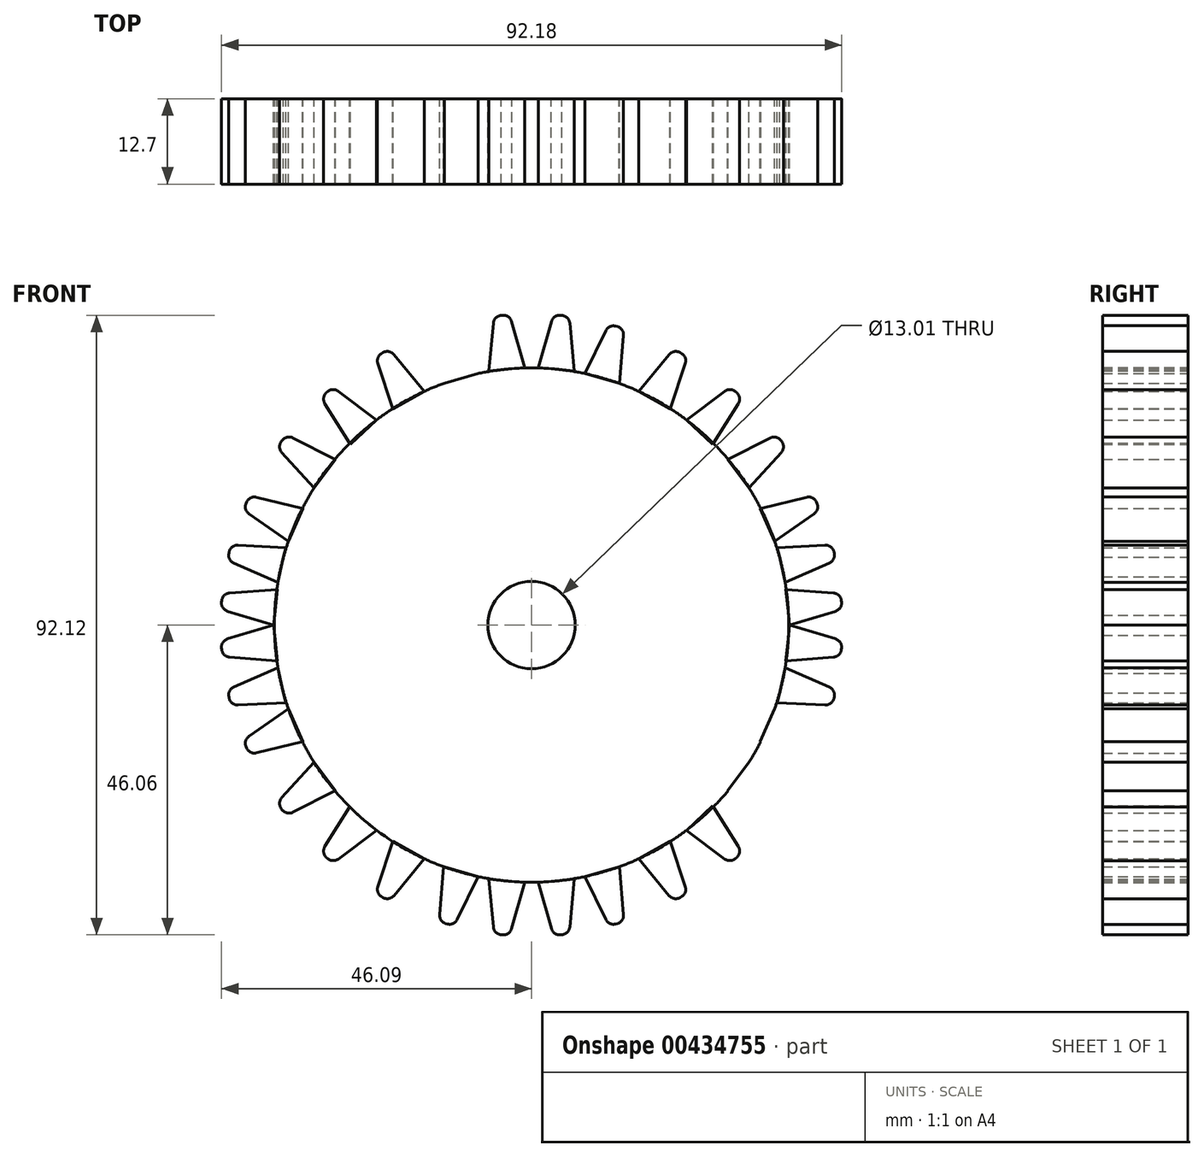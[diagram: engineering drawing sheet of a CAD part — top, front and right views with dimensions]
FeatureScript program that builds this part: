
annotation { "Feature Type Name" : "Feature", "Feature Type Description" : "" }
export const myFeature = defineFeature(function(context is Context, id is Id, definition is map)
    precondition{}
    {
        {
            var Q0;
            Q0=qCreatedBy(makeId("Front.planeOp"),FACE);
            var sketch = newSketch(context, id + "F0", { "sketchPlane" : qUnion([Q0])});
            skCircle(sketch, "E0", {"center": v(0, 0) * mm, "radius": 38.23 * mm});
            skLineSegment(sketch, "E1", {"start": v(4.32, 46.06) * mm, "end": v(4.54, 46.04) * mm});
            skLineSegment(sketch, "E2", {"start": v(5.69, 44.9) * mm, "end": v(6.35, 37.78) * mm});
            skLineSegment(sketch, "E3", {"start": v(6.35, 37.78) * mm, "end": v(1.04, 38.3) * mm});
            skLineSegment(sketch, "E4", {"start": v(1.04, 38.3) * mm, "end": v(2.98, 45.14) * mm});
            skArc(sketch, "E5.filletArc", {"start": v(4.32, 46.06) * mm, "mid": v(3.48, 45.84) * mm, "end": v(2.98, 45.14) * mm});
            skArc(sketch, "E6.filletArc", {"start": v(5.69, 44.9) * mm, "mid": v(5.32, 45.67) * mm, "end": v(4.54, 46.04) * mm});
            skLineSegment(sketch, "E7", {"start": v(-38.23, 0) * mm, "end": v(38.23, 0) * mm});
            skLineSegment(sketch, "E8", {"start": v(0, 0) * mm, "end": v(0, 38.07) * mm});
            skLineSegment(sketch, "E9", {"start": v(0, 0) * mm, "end": v(0, -38.23) * mm});
            skLineSegment(sketch, "E10", {"start": v(12.53, 44.44) * mm, "end": v(12.74, 44.38) * mm});
            skLineSegment(sketch, "E11", {"start": v(13.66, 43.05) * mm, "end": v(13.06, 35.93) * mm});
            skLineSegment(sketch, "E12", {"start": v(13.06, 35.93) * mm, "end": v(7.92, 37.38) * mm});
            skLineSegment(sketch, "E13", {"start": v(7.92, 37.38) * mm, "end": v(11.04, 43.77) * mm});
            skArc(sketch, "E14.filletArc", {"start": v(12.53, 44.44) * mm, "mid": v(11.66, 44.38) * mm, "end": v(11.04, 43.77) * mm});
            skArc(sketch, "E15.filletArc", {"start": v(13.66, 43.05) * mm, "mid": v(13.44, 43.88) * mm, "end": v(12.74, 44.38) * mm});
            skLineSegment(sketch, "E16", {"start": v(22.07, 40.52) * mm, "end": v(22.27, 40.41) * mm});
            skLineSegment(sketch, "E17", {"start": v(22.85, 38.9) * mm, "end": v(20.59, 32.13) * mm});
            skLineSegment(sketch, "E18", {"start": v(20.59, 32.13) * mm, "end": v(15.94, 34.74) * mm});
            skLineSegment(sketch, "E19", {"start": v(15.94, 34.74) * mm, "end": v(20.47, 40.23) * mm});
            skArc(sketch, "E20.filletArc", {"start": v(22.07, 40.52) * mm, "mid": v(21.22, 40.67) * mm, "end": v(20.47, 40.23) * mm});
            skArc(sketch, "E21.filletArc", {"start": v(22.85, 38.9) * mm, "mid": v(22.83, 39.76) * mm, "end": v(22.27, 40.41) * mm});
            skLineSegment(sketch, "E22", {"start": v(30.35, 34.68) * mm, "end": v(30.52, 34.53) * mm});
            skLineSegment(sketch, "E23", {"start": v(30.73, 32.92) * mm, "end": v(26.93, 26.87) * mm});
            skLineSegment(sketch, "E24", {"start": v(26.93, 26.87) * mm, "end": v(23.03, 30.51) * mm});
            skLineSegment(sketch, "E25", {"start": v(23.03, 30.51) * mm, "end": v(28.73, 34.77) * mm});
            skArc(sketch, "E26.filletArc", {"start": v(30.35, 34.68) * mm, "mid": v(29.56, 35.02) * mm, "end": v(28.73, 34.77) * mm});
            skArc(sketch, "E27.filletArc", {"start": v(30.73, 32.92) * mm, "mid": v(30.9, 33.76) * mm, "end": v(30.52, 34.53) * mm});
            skLineSegment(sketch, "E28", {"start": v(37.07, 27.46) * mm, "end": v(37.2, 27.29) * mm});
            skLineSegment(sketch, "E29", {"start": v(37.13, 25.67) * mm, "end": v(32.34, 20.38) * mm});
            skLineSegment(sketch, "E30", {"start": v(32.34, 20.38) * mm, "end": v(29.14, 24.63) * mm});
            skLineSegment(sketch, "E31", {"start": v(29.14, 24.63) * mm, "end": v(35.49, 27.83) * mm});
            skArc(sketch, "E32.filletArc", {"start": v(37.07, 27.46) * mm, "mid": v(36.35, 27.93) * mm, "end": v(35.49, 27.83) * mm});
            skArc(sketch, "E33.filletArc", {"start": v(37.13, 25.67) * mm, "mid": v(37.46, 26.47) * mm, "end": v(37.2, 27.29) * mm});
            skLineSegment(sketch, "E34", {"start": v(42.34, 18.3) * mm, "end": v(42.43, 18.1) * mm});
            skLineSegment(sketch, "E35", {"start": v(42, 16.54) * mm, "end": v(36.14, 12.44) * mm});
            skLineSegment(sketch, "E36", {"start": v(36.14, 12.44) * mm, "end": v(33.97, 17.31) * mm});
            skLineSegment(sketch, "E37", {"start": v(33.97, 17.31) * mm, "end": v(40.87, 19.01) * mm});
            skArc(sketch, "E38.filletArc", {"start": v(42.34, 18.3) * mm, "mid": v(41.73, 18.92) * mm, "end": v(40.87, 19.01) * mm});
            skArc(sketch, "E39.filletArc", {"start": v(42, 16.54) * mm, "mid": v(42.5, 17.24) * mm, "end": v(42.43, 18.1) * mm});
            skLineSegment(sketch, "E40", {"start": v(44.94, 10.9) * mm, "end": v(45, 10.68) * mm});
            skArc(sketch, "E41.filletArc", {"start": v(44.27, 9.23) * mm, "mid": v(44.9, 9.82) * mm, "end": v(45, 10.68) * mm});
            skLineSegment(sketch, "E42", {"start": v(44.27, 9.23) * mm, "end": v(37.74, 6.33) * mm});
            skLineSegment(sketch, "E43", {"start": v(37.74, 6.33) * mm, "end": v(36.54, 11.53) * mm});
            skLineSegment(sketch, "E44", {"start": v(36.54, 11.53) * mm, "end": v(43.64, 11.88) * mm});
            skArc(sketch, "E45.filletArc", {"start": v(44.94, 10.9) * mm, "mid": v(44.47, 11.62) * mm, "end": v(43.64, 11.88) * mm});
            skLineSegment(sketch, "E46", {"start": v(46.06, 3.63) * mm, "end": v(46.09, 3.4) * mm});
            skLineSegment(sketch, "E47", {"start": v(45.19, 2.06) * mm, "end": v(38.35, 0) * mm});
            skLineSegment(sketch, "E48", {"start": v(38.35, 0) * mm, "end": v(37.8, 5.3) * mm});
            skLineSegment(sketch, "E49", {"start": v(37.8, 5.3) * mm, "end": v(44.9, 4.76) * mm});
            skArc(sketch, "E50.filletArc", {"start": v(46.06, 3.63) * mm, "mid": v(45.69, 4.4) * mm, "end": v(44.9, 4.76) * mm});
            skArc(sketch, "E51.filletArc", {"start": v(45.19, 2.06) * mm, "mid": v(45.88, 2.57) * mm, "end": v(46.09, 3.4) * mm});
            skLineSegment(sketch, "E52.MirrorCS", {"start": v(-4.32, 46.06) * mm, "end": v(-4.54, 46.04) * mm});
            skArc(sketch, "E53.MirrorCS", {"start": v(-4.32, 46.06) * mm, "mid": v(-3.48, 45.84) * mm, "end": v(-2.98, 45.14) * mm});
            skLineSegment(sketch, "E54.MirrorCS", {"start": v(-1.04, 38.3) * mm, "end": v(-2.98, 45.14) * mm});
            skLineSegment(sketch, "E55.MirrorCS", {"start": v(-5.69, 44.9) * mm, "end": v(-6.35, 37.78) * mm});
            skArc(sketch, "E56.MirrorCS", {"start": v(-5.69, 44.9) * mm, "mid": v(-5.32, 45.67) * mm, "end": v(-4.54, 46.04) * mm});
            skLineSegment(sketch, "E57.MirrorCS", {"start": v(-6.35, 37.78) * mm, "end": v(-1.04, 38.3) * mm});
            skLineSegment(sketch, "E58.MirrorCS", {"start": v(-7.92, 37.38) * mm, "end": v(-11.04, 43.77) * mm});
            skArc(sketch, "E59.MirrorCS", {"start": v(-12.53, 44.44) * mm, "mid": v(-11.66, 44.38) * mm, "end": v(-11.04, 43.77) * mm});
            skArc(sketch, "E60.MirrorCS", {"start": v(-13.66, 43.05) * mm, "mid": v(-13.44, 43.88) * mm, "end": v(-12.74, 44.38) * mm});
            skLineSegment(sketch, "E61.MirrorCS", {"start": v(-13.66, 43.05) * mm, "end": v(-13.06, 35.93) * mm});
            skLineSegment(sketch, "E62.MirrorCS", {"start": v(-13.06, 35.93) * mm, "end": v(-7.92, 37.38) * mm});
            skLineSegment(sketch, "E63.MirrorCS", {"start": v(-12.53, 44.44) * mm, "end": v(-12.74, 44.38) * mm});
            skLineSegment(sketch, "E64.MirrorCS", {"start": v(-22.07, 40.52) * mm, "end": v(-22.27, 40.41) * mm});
            skArc(sketch, "E65.MirrorCS", {"start": v(-22.07, 40.52) * mm, "mid": v(-21.22, 40.67) * mm, "end": v(-20.47, 40.23) * mm});
            skArc(sketch, "E66.MirrorCS", {"start": v(-22.85, 38.9) * mm, "mid": v(-22.83, 39.76) * mm, "end": v(-22.27, 40.41) * mm});
            skLineSegment(sketch, "E67.MirrorCS", {"start": v(-22.85, 38.9) * mm, "end": v(-20.59, 32.13) * mm});
            skLineSegment(sketch, "E68.MirrorCS", {"start": v(-15.94, 34.74) * mm, "end": v(-20.47, 40.23) * mm});
            skLineSegment(sketch, "E69.MirrorCS", {"start": v(-20.59, 32.13) * mm, "end": v(-15.94, 34.74) * mm});
            skLineSegment(sketch, "E70.MirrorCS", {"start": v(-30.35, 34.68) * mm, "end": v(-30.52, 34.53) * mm});
            skArc(sketch, "E71.MirrorCS", {"start": v(-30.35, 34.68) * mm, "mid": v(-29.56, 35.02) * mm, "end": v(-28.73, 34.77) * mm});
            skArc(sketch, "E72.MirrorCS", {"start": v(-30.73, 32.92) * mm, "mid": v(-30.9, 33.76) * mm, "end": v(-30.52, 34.53) * mm});
            skLineSegment(sketch, "E73.MirrorCS", {"start": v(-30.73, 32.92) * mm, "end": v(-26.93, 26.87) * mm});
            skLineSegment(sketch, "E74.MirrorCS", {"start": v(-23.03, 30.51) * mm, "end": v(-28.73, 34.77) * mm});
            skLineSegment(sketch, "E75.MirrorCS", {"start": v(-37.13, 25.67) * mm, "end": v(-32.34, 20.38) * mm});
            skLineSegment(sketch, "E76.MirrorCS", {"start": v(-29.14, 24.63) * mm, "end": v(-35.49, 27.83) * mm});
            skArc(sketch, "E77.MirrorCS", {"start": v(-37.07, 27.46) * mm, "mid": v(-36.35, 27.93) * mm, "end": v(-35.49, 27.83) * mm});
            skArc(sketch, "E78.MirrorCS", {"start": v(-37.13, 25.67) * mm, "mid": v(-37.46, 26.47) * mm, "end": v(-37.2, 27.29) * mm});
            skLineSegment(sketch, "E79.MirrorCS", {"start": v(-32.34, 20.38) * mm, "end": v(-29.14, 24.63) * mm});
            skLineSegment(sketch, "E80.MirrorCS", {"start": v(-37.07, 27.46) * mm, "end": v(-37.2, 27.29) * mm});
            skLineSegment(sketch, "E81.MirrorCS", {"start": v(-33.97, 17.31) * mm, "end": v(-40.87, 19.01) * mm});
            skLineSegment(sketch, "E82.MirrorCS", {"start": v(-36.54, 11.53) * mm, "end": v(-43.64, 11.88) * mm});
            skLineSegment(sketch, "E83.MirrorCS", {"start": v(-37.8, 5.3) * mm, "end": v(-44.9, 4.76) * mm});
            skLineSegment(sketch, "E84.MirrorCS", {"start": v(-42.34, 18.3) * mm, "end": v(-42.43, 18.1) * mm});
            skArc(sketch, "E85.MirrorCS", {"start": v(-42, 16.54) * mm, "mid": v(-42.5, 17.24) * mm, "end": v(-42.43, 18.1) * mm});
            skArc(sketch, "E86.MirrorCS", {"start": v(-42.34, 18.3) * mm, "mid": v(-41.73, 18.92) * mm, "end": v(-40.87, 19.01) * mm});
            skLineSegment(sketch, "E87.MirrorCS", {"start": v(-42, 16.54) * mm, "end": v(-36.14, 12.44) * mm});
            skLineSegment(sketch, "E88.MirrorCS", {"start": v(-44.27, 9.23) * mm, "end": v(-37.74, 6.33) * mm});
            skArc(sketch, "E89.MirrorCS", {"start": v(-44.94, 10.9) * mm, "mid": v(-44.47, 11.62) * mm, "end": v(-43.64, 11.88) * mm});
            skArc(sketch, "E90.MirrorCS", {"start": v(-44.27, 9.23) * mm, "mid": v(-44.9, 9.82) * mm, "end": v(-45, 10.68) * mm});
            skLineSegment(sketch, "E91.MirrorCS", {"start": v(-44.94, 10.9) * mm, "end": v(-45, 10.68) * mm});
            skLineSegment(sketch, "E92.MirrorCS", {"start": v(-37.74, 6.33) * mm, "end": v(-36.54, 11.53) * mm});
            skLineSegment(sketch, "E93.MirrorCS", {"start": v(-45.19, 2.06) * mm, "end": v(-38.35, 0) * mm});
            skArc(sketch, "E94.MirrorCS", {"start": v(-45.19, 2.06) * mm, "mid": v(-45.88, 2.57) * mm, "end": v(-46.09, 3.4) * mm});
            skArc(sketch, "E95.MirrorCS", {"start": v(-46.06, 3.63) * mm, "mid": v(-45.69, 4.4) * mm, "end": v(-44.9, 4.76) * mm});
            skLineSegment(sketch, "E96.MirrorCS", {"start": v(-46.06, 3.63) * mm, "end": v(-46.09, 3.4) * mm});
            skLineSegment(sketch, "E97.MirrorCS", {"start": v(-38.35, 0) * mm, "end": v(-37.8, 5.3) * mm});
            skLineSegment(sketch, "E98.MirrorCS", {"start": v(-37.8, -5.3) * mm, "end": v(-44.9, -4.76) * mm});
            skLineSegment(sketch, "E99.MirrorCS", {"start": v(-45.19, -2.06) * mm, "end": v(-38.35, 0) * mm});
            skArc(sketch, "E100.MirrorCS", {"start": v(-45.19, -2.06) * mm, "mid": v(-45.88, -2.57) * mm, "end": v(-46.09, -3.4) * mm});
            skArc(sketch, "E101.MirrorCS", {"start": v(-46.06, -3.63) * mm, "mid": v(-45.69, -4.4) * mm, "end": v(-44.9, -4.76) * mm});
            skLineSegment(sketch, "E102.MirrorCS", {"start": v(-46.06, -3.63) * mm, "end": v(-46.09, -3.4) * mm});
            skLineSegment(sketch, "E103.MirrorCS", {"start": v(-44.94, -10.9) * mm, "end": v(-45, -10.68) * mm});
            skArc(sketch, "E104.MirrorCS", {"start": v(-44.27, -9.23) * mm, "mid": v(-44.9, -9.82) * mm, "end": v(-45, -10.68) * mm});
            skLineSegment(sketch, "E105.MirrorCS", {"start": v(-44.27, -9.23) * mm, "end": v(-37.74, -6.33) * mm});
            skLineSegment(sketch, "E106.MirrorCS", {"start": v(-36.54, -11.53) * mm, "end": v(-43.64, -11.88) * mm});
            skArc(sketch, "E107.MirrorCS", {"start": v(-44.94, -10.9) * mm, "mid": v(-44.47, -11.62) * mm, "end": v(-43.64, -11.88) * mm});
            skLineSegment(sketch, "E108.MirrorCS", {"start": v(-37.74, -6.33) * mm, "end": v(-36.54, -11.53) * mm});
            skLineSegment(sketch, "E109.MirrorCS", {"start": v(-42, -16.54) * mm, "end": v(-36.14, -12.44) * mm});
            skArc(sketch, "E110.MirrorCS", {"start": v(-42, -16.54) * mm, "mid": v(-42.5, -17.24) * mm, "end": v(-42.43, -18.1) * mm});
            skArc(sketch, "E111.MirrorCS", {"start": v(-42.34, -18.3) * mm, "mid": v(-41.73, -18.92) * mm, "end": v(-40.87, -19.01) * mm});
            skLineSegment(sketch, "E112.MirrorCS", {"start": v(-33.97, -17.31) * mm, "end": v(-40.87, -19.01) * mm});
            skLineSegment(sketch, "E113.MirrorCS", {"start": v(-42.34, -18.3) * mm, "end": v(-42.43, -18.1) * mm});
            skLineSegment(sketch, "E114.MirrorCS", {"start": v(-32.34, -20.38) * mm, "end": v(-29.14, -24.63) * mm});
            skLineSegment(sketch, "E115.MirrorCS", {"start": v(-37.13, -25.67) * mm, "end": v(-32.34, -20.38) * mm});
            skLineSegment(sketch, "E116.MirrorCS", {"start": v(-29.14, -24.63) * mm, "end": v(-35.49, -27.83) * mm});
            skArc(sketch, "E117.MirrorCS", {"start": v(-37.13, -25.67) * mm, "mid": v(-37.46, -26.47) * mm, "end": v(-37.2, -27.29) * mm});
            skArc(sketch, "E118.MirrorCS", {"start": v(-37.07, -27.46) * mm, "mid": v(-36.35, -27.93) * mm, "end": v(-35.49, -27.83) * mm});
            skLineSegment(sketch, "E119.MirrorCS", {"start": v(-37.07, -27.46) * mm, "end": v(-37.2, -27.29) * mm});
            skLineSegment(sketch, "E120.MirrorCS", {"start": v(-30.73, -32.92) * mm, "end": v(-26.93, -26.87) * mm});
            skArc(sketch, "E121.MirrorCS", {"start": v(-30.73, -32.92) * mm, "mid": v(-30.9, -33.76) * mm, "end": v(-30.52, -34.53) * mm});
            skArc(sketch, "E122.MirrorCS", {"start": v(-30.35, -34.68) * mm, "mid": v(-29.56, -35.02) * mm, "end": v(-28.73, -34.77) * mm});
            skLineSegment(sketch, "E123.MirrorCS", {"start": v(-23.03, -30.51) * mm, "end": v(-28.73, -34.77) * mm});
            skLineSegment(sketch, "E124.MirrorCS", {"start": v(-20.59, -32.13) * mm, "end": v(-15.94, -34.74) * mm});
            skLineSegment(sketch, "E125.MirrorCS", {"start": v(-22.85, -38.9) * mm, "end": v(-20.59, -32.13) * mm});
            skLineSegment(sketch, "E126.MirrorCS", {"start": v(-15.94, -34.74) * mm, "end": v(-20.47, -40.23) * mm});
            skArc(sketch, "E127.MirrorCS", {"start": v(-22.07, -40.52) * mm, "mid": v(-21.22, -40.67) * mm, "end": v(-20.47, -40.23) * mm});
            skArc(sketch, "E128.MirrorCS", {"start": v(-22.85, -38.9) * mm, "mid": v(-22.83, -39.76) * mm, "end": v(-22.27, -40.41) * mm});
            skLineSegment(sketch, "E129.MirrorCS", {"start": v(-22.07, -40.52) * mm, "end": v(-22.27, -40.41) * mm});
            skLineSegment(sketch, "E130.MirrorCS", {"start": v(-13.66, -43.05) * mm, "end": v(-13.06, -35.93) * mm});
            skArc(sketch, "E131.MirrorCS", {"start": v(-13.66, -43.05) * mm, "mid": v(-13.44, -43.88) * mm, "end": v(-12.74, -44.38) * mm});
            skArc(sketch, "E132.MirrorCS", {"start": v(-12.53, -44.44) * mm, "mid": v(-11.66, -44.38) * mm, "end": v(-11.04, -43.77) * mm});
            skLineSegment(sketch, "E133.MirrorCS", {"start": v(-7.92, -37.38) * mm, "end": v(-11.04, -43.77) * mm});
            skLineSegment(sketch, "E134.MirrorCS", {"start": v(-13.06, -35.93) * mm, "end": v(-7.92, -37.38) * mm});
            skLineSegment(sketch, "E135.MirrorCS", {"start": v(-5.69, -44.9) * mm, "end": v(-6.35, -37.78) * mm});
            skLineSegment(sketch, "E136.MirrorCS", {"start": v(-1.04, -38.3) * mm, "end": v(-2.98, -45.14) * mm});
            skLineSegment(sketch, "E137.MirrorCS", {"start": v(-12.53, -44.44) * mm, "end": v(-12.74, -44.38) * mm});
            skLineSegment(sketch, "E138.MirrorCS", {"start": v(-4.32, -46.06) * mm, "end": v(-4.54, -46.04) * mm});
            skArc(sketch, "E139.MirrorCS", {"start": v(-4.32, -46.06) * mm, "mid": v(-3.48, -45.84) * mm, "end": v(-2.98, -45.14) * mm});
            skArc(sketch, "E140.MirrorCS", {"start": v(-5.69, -44.9) * mm, "mid": v(-5.32, -45.67) * mm, "end": v(-4.54, -46.04) * mm});
            skLineSegment(sketch, "E141.MirrorCS", {"start": v(-6.35, -37.78) * mm, "end": v(-1.04, -38.3) * mm});
            skLineSegment(sketch, "E142.MirrorCS", {"start": v(-30.35, -34.68) * mm, "end": v(-30.52, -34.53) * mm});
            skLineSegment(sketch, "E143.MirrorCS", {"start": v(-26.93, 26.87) * mm, "end": v(-23.03, 30.51) * mm});
            skLineSegment(sketch, "E144.MirrorCS", {"start": v(-36.14, 12.44) * mm, "end": v(-33.97, 17.31) * mm});
            skLineSegment(sketch, "E145.MirrorCS", {"start": v(-36.14, -12.44) * mm, "end": v(-33.97, -17.31) * mm});
            skLineSegment(sketch, "E146.MirrorCS", {"start": v(-38.35, 0) * mm, "end": v(-37.8, -5.3) * mm});
            skLineSegment(sketch, "E147.MirrorCS", {"start": v(5.69, -44.9) * mm, "end": v(6.35, -37.78) * mm});
            skLineSegment(sketch, "E148.MirrorCS", {"start": v(1.04, -38.3) * mm, "end": v(2.98, -45.14) * mm});
            skArc(sketch, "E149.MirrorCS", {"start": v(4.32, -46.06) * mm, "mid": v(3.48, -45.84) * mm, "end": v(2.98, -45.14) * mm});
            skLineSegment(sketch, "E150.MirrorCS", {"start": v(4.32, -46.06) * mm, "end": v(4.54, -46.04) * mm});
            skArc(sketch, "E151.MirrorCS", {"start": v(5.69, -44.9) * mm, "mid": v(5.32, -45.67) * mm, "end": v(4.54, -46.04) * mm});
            skLineSegment(sketch, "E152.MirrorCS", {"start": v(13.66, -43.05) * mm, "end": v(13.06, -35.93) * mm});
            skLineSegment(sketch, "E153.MirrorCS", {"start": v(6.35, -37.78) * mm, "end": v(1.04, -38.3) * mm});
            skLineSegment(sketch, "E154.MirrorCS", {"start": v(7.92, -37.38) * mm, "end": v(11.04, -43.77) * mm});
            skArc(sketch, "E155.MirrorCS", {"start": v(12.53, -44.44) * mm, "mid": v(11.66, -44.38) * mm, "end": v(11.04, -43.77) * mm});
            skArc(sketch, "E156.MirrorCS", {"start": v(13.66, -43.05) * mm, "mid": v(13.44, -43.88) * mm, "end": v(12.74, -44.38) * mm});
            skLineSegment(sketch, "E157.MirrorCS", {"start": v(12.53, -44.44) * mm, "end": v(12.74, -44.38) * mm});
            skLineSegment(sketch, "E158.MirrorCS", {"start": v(13.06, -35.93) * mm, "end": v(7.92, -37.38) * mm});
            skLineSegment(sketch, "E159.MirrorCS", {"start": v(15.94, -34.74) * mm, "end": v(20.47, -40.23) * mm});
            skArc(sketch, "E160.MirrorCS", {"start": v(22.07, -40.52) * mm, "mid": v(21.22, -40.67) * mm, "end": v(20.47, -40.23) * mm});
            skArc(sketch, "E161.MirrorCS", {"start": v(22.85, -38.9) * mm, "mid": v(22.83, -39.76) * mm, "end": v(22.27, -40.41) * mm});
            skLineSegment(sketch, "E162.MirrorCS", {"start": v(22.85, -38.9) * mm, "end": v(20.59, -32.13) * mm});
            skLineSegment(sketch, "E163.MirrorCS", {"start": v(20.59, -32.13) * mm, "end": v(15.94, -34.74) * mm});
            skLineSegment(sketch, "E164.MirrorCS", {"start": v(22.07, -40.52) * mm, "end": v(22.27, -40.41) * mm});
            skLineSegment(sketch, "E165.MirrorCS", {"start": v(30.73, -32.92) * mm, "end": v(26.93, -26.87) * mm});
            skLineSegment(sketch, "E166.MirrorCS", {"start": v(23.03, -30.51) * mm, "end": v(28.73, -34.77) * mm});
            skArc(sketch, "E167.MirrorCS", {"start": v(30.35, -34.68) * mm, "mid": v(29.56, -35.02) * mm, "end": v(28.73, -34.77) * mm});
            skArc(sketch, "E168.MirrorCS", {"start": v(30.73, -32.92) * mm, "mid": v(30.9, -33.76) * mm, "end": v(30.52, -34.53) * mm});
            skLineSegment(sketch, "E169.MirrorCS", {"start": v(26.93, -26.87) * mm, "end": v(23.03, -30.51) * mm});
            skLineSegment(sketch, "E170.MirrorCS", {"start": v(30.35, -34.68) * mm, "end": v(30.52, -34.53) * mm});
            skLineSegment(sketch, "E171.MirrorCS", {"start": v(29.14, -24.63) * mm, "end": v(35.49, -27.83) * mm});
            skArc(sketch, "E172.MirrorCS", {"start": v(37.07, -27.46) * mm, "mid": v(36.35, -27.93) * mm, "end": v(35.49, -27.83) * mm});
            skArc(sketch, "E173.MirrorCS", {"start": v(37.13, -25.67) * mm, "mid": v(37.46, -26.47) * mm, "end": v(37.2, -27.29) * mm});
            skLineSegment(sketch, "E174.MirrorCS", {"start": v(37.13, -25.67) * mm, "end": v(32.34, -20.38) * mm});
            skLineSegment(sketch, "E175.MirrorCS", {"start": v(32.34, -20.38) * mm, "end": v(29.14, -24.63) * mm});
            skLineSegment(sketch, "E176.MirrorCS", {"start": v(37.07, -27.46) * mm, "end": v(37.2, -27.29) * mm});
            skArc(sketch, "E177.MirrorCS", {"start": v(42, -16.54) * mm, "mid": v(42.5, -17.24) * mm, "end": v(42.43, -18.1) * mm});
            skArc(sketch, "E178.MirrorCS", {"start": v(42.34, -18.3) * mm, "mid": v(41.73, -18.92) * mm, "end": v(40.87, -19.01) * mm});
            skLineSegment(sketch, "E179.MirrorCS", {"start": v(33.97, -17.31) * mm, "end": v(40.87, -19.01) * mm});
            skLineSegment(sketch, "E180.MirrorCS", {"start": v(42, -16.54) * mm, "end": v(36.14, -12.44) * mm});
            skLineSegment(sketch, "E181.MirrorCS", {"start": v(36.14, -12.44) * mm, "end": v(33.97, -17.31) * mm});
            skLineSegment(sketch, "E182.MirrorCS", {"start": v(42.34, -18.3) * mm, "end": v(42.43, -18.1) * mm});
            skLineSegment(sketch, "E183.MirrorCS", {"start": v(37.74, -6.33) * mm, "end": v(36.54, -11.53) * mm});
            skLineSegment(sketch, "E184.MirrorCS", {"start": v(36.54, -11.53) * mm, "end": v(43.64, -11.88) * mm});
            skLineSegment(sketch, "E185.MirrorCS", {"start": v(44.27, -9.23) * mm, "end": v(37.74, -6.33) * mm});
            skArc(sketch, "E186.MirrorCS", {"start": v(44.27, -9.23) * mm, "mid": v(44.9, -9.82) * mm, "end": v(45, -10.68) * mm});
            skArc(sketch, "E187.MirrorCS", {"start": v(44.94, -10.9) * mm, "mid": v(44.47, -11.62) * mm, "end": v(43.64, -11.88) * mm});
            skLineSegment(sketch, "E188.MirrorCS", {"start": v(44.94, -10.9) * mm, "end": v(45, -10.68) * mm});
            skLineSegment(sketch, "E189.MirrorCS", {"start": v(45.19, -2.06) * mm, "end": v(38.35, 0) * mm});
            skLineSegment(sketch, "E190.MirrorCS", {"start": v(38.35, 0) * mm, "end": v(37.8, -5.3) * mm});
            skArc(sketch, "E191.MirrorCS", {"start": v(45.19, -2.06) * mm, "mid": v(45.88, -2.57) * mm, "end": v(46.09, -3.4) * mm});
            skArc(sketch, "E192.MirrorCS", {"start": v(46.06, -3.63) * mm, "mid": v(45.69, -4.4) * mm, "end": v(44.9, -4.76) * mm});
            skLineSegment(sketch, "E193.MirrorCS", {"start": v(37.8, -5.3) * mm, "end": v(44.9, -4.76) * mm});
            skLineSegment(sketch, "E194.MirrorCS", {"start": v(46.06, -3.63) * mm, "end": v(46.09, -3.4) * mm});
            skCircle(sketch, "E195", {"center": v(0, 0) * mm, "radius": 6.5 * mm});
            skSolve(sketch);
        }
        {
            var Q0;
            {var subQ15=sQuery(id+"F0.wireOp",EDGE,"E18");Q0=makeQuery(id+"F0.imprint","IMPRINT",FACE,{"disambiguationData":[TD([[makeQuery(id+"F0.imprint","IMPRINT",EDGE,{"derivedFrom":subQ15}),1.0]])]});}
            var Q1;
            {var subQ5=sQuery(id+"F0.wireOp",EDGE,"E114.MirrorCS");Q1=makeQuery(id+"F0.imprint","IMPRINT",FACE,{"disambiguationData":[TD([[makeQuery(id+"F0.imprint","IMPRINT",EDGE,{"derivedFrom":subQ5}),1.0]])]});}
            var Q2;
            {var subQ7=sQuery(id+"F0.wireOp",EDGE,"E163.MirrorCS");Q2=makeQuery(id+"F0.imprint","IMPRINT",FACE,{"disambiguationData":[TD([[makeQuery(id+"F0.imprint","IMPRINT",EDGE,{"derivedFrom":subQ7}),-1.0]])]});}
            var Q3;
            {var subQ0=sQuery(id+"F0.wireOp",EDGE,"E8");var subQ1=sQuery(id+"F0.wireOp",EDGE,"i3N7d21D-9b7o-vpFr-M5c5-Z3wWhtBlQD8E");var subQ2=makeQuery(id+"F0.imprint","INTERSECT",VERTEX,{"derivedFrom":[subQ1,subQ0]});Q3=makeQuery(id+"F0.imprint","IMPRINT",FACE,{"disambiguationData":[TD([[makeQuery(id+"F0.imprint","IMPRINT",EDGE,{"disambiguationData":[TD([[subQ2,1.0]])],"derivedFrom":subQ1}),1.0]])]});}
            var Q4;
            {var subQ0=sQuery(id+"F0.wireOp",EDGE,"E8");var subQ1=sQuery(id+"F0.wireOp",EDGE,"i3N7d21D-9b7o-vpFr-M5c5-Z3wWhtBlQD8E");var subQ2=makeQuery(id+"F0.imprint","INTERSECT",VERTEX,{"derivedFrom":[subQ1,subQ0]});Q4=makeQuery(id+"F0.imprint","IMPRINT",FACE,{"disambiguationData":[TD([[makeQuery(id+"F0.imprint","IMPRINT",EDGE,{"disambiguationData":[TD([[subQ2,-1.0]])],"derivedFrom":subQ1}),1.0]])]});}
            var Q5;
            {var subQ0=sQuery(id+"F0.wireOp",EDGE,"E7");var subQ1=sQuery(id+"F0.wireOp",EDGE,"i3N7d21D-9b7o-vpFr-M5c5-Z3wWhtBlQD8E");var subQ2=makeQuery(id+"F0.imprint","INTERSECT",VERTEX,{"disambiguationData":[OD(1.0)],"derivedFrom":[subQ1,subQ0]});Q5=makeQuery(id+"F0.imprint","IMPRINT",FACE,{"disambiguationData":[TD([[makeQuery(id+"F0.imprint","IMPRINT",EDGE,{"disambiguationData":[TD([[subQ2,-1.0]])],"derivedFrom":subQ1}),1.0]])]});}
            var Q6;
            {var subQ0=sQuery(id+"F0.wireOp",EDGE,"E7");var subQ1=sQuery(id+"F0.wireOp",EDGE,"i3N7d21D-9b7o-vpFr-M5c5-Z3wWhtBlQD8E");var subQ2=makeQuery(id+"F0.imprint","INTERSECT",VERTEX,{"disambiguationData":[OD(0.0)],"derivedFrom":[subQ1,subQ0]});Q6=makeQuery(id+"F0.imprint","IMPRINT",FACE,{"disambiguationData":[TD([[makeQuery(id+"F0.imprint","IMPRINT",EDGE,{"disambiguationData":[TD([[subQ2,1.0]])],"derivedFrom":subQ1}),1.0]])]});}
            extrude(context, id + "F1", {"entities" : qUnion([Q0, Q1, Q2, Q3, Q4, Q5, Q6]), "depth" : 12.7 * mm});
        }
        {
            var Q0;
            Q0=makeQuery(id+"F0.imprint","IMPRINT",FACE,{"disambiguationData":[TD([[makeQuery(id+"F0.imprint","IMPRINT",EDGE,{"derivedFrom":sQuery(id+"F0.wireOp",EDGE,"E10")}),-1.0]])]});
            var Q1;
            Q1=makeQuery(id+"F0.imprint","IMPRINT",FACE,{"disambiguationData":[TD([[makeQuery(id+"F0.imprint","IMPRINT",EDGE,{"derivedFrom":sQuery(id+"F0.wireOp",EDGE,"E1")}),-1.0]])]});
            var Q2;
            Q2=makeQuery(id+"F0.imprint","IMPRINT",FACE,{"disambiguationData":[TD([[makeQuery(id+"F0.imprint","IMPRINT",EDGE,{"derivedFrom":sQuery(id+"F0.wireOp",EDGE,"E52.MirrorCS")}),1.0]])]});
            var Q3;
            {var subQ1=sQuery(id+"F0.wireOp",EDGE,"E59.MirrorCS");Q3=makeQuery(id+"F0.imprint","IMPRINT",FACE,{"disambiguationData":[TD([[makeQuery(id+"F0.imprint","IMPRINT",EDGE,{"derivedFrom":subQ1}),-1.0]])]});}
            var Q4;
            Q4=makeQuery(id+"F0.imprint","IMPRINT",FACE,{"disambiguationData":[TD([[makeQuery(id+"F0.imprint","IMPRINT",EDGE,{"derivedFrom":sQuery(id+"F0.wireOp",EDGE,"E64.MirrorCS")}),1.0]])]});
            var Q5;
            Q5=makeQuery(id+"F0.imprint","IMPRINT",FACE,{"disambiguationData":[TD([[makeQuery(id+"F0.imprint","IMPRINT",EDGE,{"derivedFrom":sQuery(id+"F0.wireOp",EDGE,"E70.MirrorCS")}),1.0]])]});
            var Q6;
            {var subQ4=sQuery(id+"F0.wireOp",EDGE,"E75.MirrorCS");Q6=makeQuery(id+"F0.imprint","IMPRINT",FACE,{"disambiguationData":[TD([[makeQuery(id+"F0.imprint","IMPRINT",EDGE,{"derivedFrom":subQ4}),1.0]])]});}
            var Q7;
            Q7=makeQuery(id+"F0.imprint","IMPRINT",FACE,{"disambiguationData":[TD([[makeQuery(id+"F0.imprint","IMPRINT",EDGE,{"derivedFrom":sQuery(id+"F0.wireOp",EDGE,"E84.MirrorCS")}),1.0]])]});
            var Q8;
            {var subQ1=sQuery(id+"F0.wireOp",EDGE,"E82.MirrorCS");Q8=makeQuery(id+"F0.imprint","IMPRINT",FACE,{"disambiguationData":[TD([[makeQuery(id+"F0.imprint","IMPRINT",EDGE,{"derivedFrom":subQ1}),1.0]])]});}
            var Q9;
            {var subQ0=sQuery(id+"F0.wireOp",EDGE,"E93.MirrorCS");Q9=makeQuery(id+"F0.imprint","IMPRINT",FACE,{"disambiguationData":[TD([[makeQuery(id+"F0.imprint","IMPRINT",EDGE,{"derivedFrom":subQ0}),1.0]])]});}
            var Q10;
            {var subQ5=sQuery(id+"F0.wireOp",EDGE,"E99.MirrorCS");Q10=makeQuery(id+"F0.imprint","IMPRINT",FACE,{"disambiguationData":[TD([[makeQuery(id+"F0.imprint","IMPRINT",EDGE,{"derivedFrom":subQ5}),-1.0]])]});}
            var Q11;
            Q11=makeQuery(id+"F0.imprint","IMPRINT",FACE,{"disambiguationData":[TD([[makeQuery(id+"F0.imprint","IMPRINT",EDGE,{"derivedFrom":sQuery(id+"F0.wireOp",EDGE,"E103.MirrorCS")}),-1.0]])]});
            var Q12;
            {var subQ0=sQuery(id+"F0.wireOp",EDGE,"E109.MirrorCS");Q12=makeQuery(id+"F0.imprint","IMPRINT",FACE,{"disambiguationData":[TD([[makeQuery(id+"F0.imprint","IMPRINT",EDGE,{"derivedFrom":subQ0}),-1.0]])]});}
            var Q13;
            {var subQ4=sQuery(id+"F0.wireOp",EDGE,"E115.MirrorCS");Q13=makeQuery(id+"F0.imprint","IMPRINT",FACE,{"disambiguationData":[TD([[makeQuery(id+"F0.imprint","IMPRINT",EDGE,{"derivedFrom":subQ4}),-1.0]])]});}
            var Q14;
            {var subQ0=sQuery(id+"F0.wireOp",EDGE,"E121.MirrorCS");Q14=makeQuery(id+"F0.imprint","IMPRINT",FACE,{"disambiguationData":[TD([[makeQuery(id+"F0.imprint","IMPRINT",EDGE,{"derivedFrom":subQ0}),1.0]])]});}
            var Q15;
            {var subQ0=sQuery(id+"F0.wireOp",EDGE,"E126.MirrorCS");Q15=makeQuery(id+"F0.imprint","IMPRINT",FACE,{"disambiguationData":[TD([[makeQuery(id+"F0.imprint","IMPRINT",EDGE,{"derivedFrom":subQ0}),-1.0]])]});}
            var Q16;
            {var subQ1=sQuery(id+"F0.wireOp",EDGE,"E130.MirrorCS");Q16=makeQuery(id+"F0.imprint","IMPRINT",FACE,{"disambiguationData":[TD([[makeQuery(id+"F0.imprint","IMPRINT",EDGE,{"derivedFrom":subQ1}),-1.0]])]});}
            var Q17;
            {var subQ1=sQuery(id+"F0.wireOp",EDGE,"E135.MirrorCS");Q17=makeQuery(id+"F0.imprint","IMPRINT",FACE,{"disambiguationData":[TD([[makeQuery(id+"F0.imprint","IMPRINT",EDGE,{"derivedFrom":subQ1}),-1.0]])]});}
            var Q18;
            {var subQ1=sQuery(id+"F0.wireOp",EDGE,"E147.MirrorCS");Q18=makeQuery(id+"F0.imprint","IMPRINT",FACE,{"disambiguationData":[TD([[makeQuery(id+"F0.imprint","IMPRINT",EDGE,{"derivedFrom":subQ1}),1.0]])]});}
            var Q19;
            {var subQ4=sQuery(id+"F0.wireOp",EDGE,"E152.MirrorCS");Q19=makeQuery(id+"F0.imprint","IMPRINT",FACE,{"disambiguationData":[TD([[makeQuery(id+"F0.imprint","IMPRINT",EDGE,{"derivedFrom":subQ4}),1.0]])]});}
            var Q20;
            {var subQ1=sQuery(id+"F0.wireOp",EDGE,"E159.MirrorCS");Q20=makeQuery(id+"F0.imprint","IMPRINT",FACE,{"disambiguationData":[TD([[makeQuery(id+"F0.imprint","IMPRINT",EDGE,{"derivedFrom":subQ1}),1.0]])]});}
            var Q21;
            {var subQ0=sQuery(id+"F0.wireOp",EDGE,"E166.MirrorCS");Q21=makeQuery(id+"F0.imprint","IMPRINT",FACE,{"disambiguationData":[TD([[makeQuery(id+"F0.imprint","IMPRINT",EDGE,{"derivedFrom":subQ0}),1.0]])]});}
            var Q22;
            {var subQ0=sQuery(id+"F0.wireOp",EDGE,"E172.MirrorCS");Q22=makeQuery(id+"F0.imprint","IMPRINT",FACE,{"disambiguationData":[TD([[makeQuery(id+"F0.imprint","IMPRINT",EDGE,{"derivedFrom":subQ0}),-1.0]])]});}
            var Q23;
            Q23=makeQuery(id+"F0.imprint","IMPRINT",FACE,{"disambiguationData":[TD([[makeQuery(id+"F0.imprint","IMPRINT",EDGE,{"derivedFrom":sQuery(id+"F0.wireOp",EDGE,"E177.MirrorCS")}),-1.0]])]});
            var Q24;
            {var subQ0=sQuery(id+"F0.wireOp",EDGE,"E184.MirrorCS");Q24=makeQuery(id+"F0.imprint","IMPRINT",FACE,{"disambiguationData":[TD([[makeQuery(id+"F0.imprint","IMPRINT",EDGE,{"derivedFrom":subQ0}),1.0]])]});}
            var Q25;
            {var subQ5=sQuery(id+"F0.wireOp",EDGE,"E189.MirrorCS");Q25=makeQuery(id+"F0.imprint","IMPRINT",FACE,{"disambiguationData":[TD([[makeQuery(id+"F0.imprint","IMPRINT",EDGE,{"derivedFrom":subQ5}),1.0]])]});}
            var Q26;
            Q26=makeQuery(id+"F0.imprint","IMPRINT",FACE,{"disambiguationData":[TD([[makeQuery(id+"F0.imprint","IMPRINT",EDGE,{"derivedFrom":sQuery(id+"F0.wireOp",EDGE,"E46")}),-1.0]])]});
            var Q27;
            Q27=makeQuery(id+"F0.imprint","IMPRINT",FACE,{"disambiguationData":[TD([[makeQuery(id+"F0.imprint","IMPRINT",EDGE,{"derivedFrom":sQuery(id+"F0.wireOp",EDGE,"E40")}),-1.0]])]});
            var Q28;
            Q28=makeQuery(id+"F0.imprint","IMPRINT",FACE,{"disambiguationData":[TD([[makeQuery(id+"F0.imprint","IMPRINT",EDGE,{"derivedFrom":sQuery(id+"F0.wireOp",EDGE,"E34")}),-1.0]])]});
            var Q29;
            Q29=makeQuery(id+"F0.imprint","IMPRINT",FACE,{"disambiguationData":[TD([[makeQuery(id+"F0.imprint","IMPRINT",EDGE,{"derivedFrom":sQuery(id+"F0.wireOp",EDGE,"E28")}),-1.0]])]});
            var Q30;
            Q30=makeQuery(id+"F0.imprint","IMPRINT",FACE,{"disambiguationData":[TD([[makeQuery(id+"F0.imprint","IMPRINT",EDGE,{"derivedFrom":sQuery(id+"F0.wireOp",EDGE,"E16")}),-1.0]])]});
            var Q31;
            Q31=makeQuery(id+"F0.imprint","IMPRINT",FACE,{"disambiguationData":[TD([[makeQuery(id+"F0.imprint","IMPRINT",EDGE,{"derivedFrom":sQuery(id+"F0.wireOp",EDGE,"E22")}),-1.0]])]});
            extrude(context, id + "F2", {"entities" : qUnion([Q0, Q1, Q2, Q3, Q4, Q5, Q6, Q7, Q8, Q9, Q10, Q11, Q12, Q13, Q14, Q15, Q16, Q17, Q18, Q19, Q20, Q21, Q22, Q23, Q24, Q25, Q26, Q27, Q28, Q29, Q30, Q31]), "depth" : 12.7 * mm});
        }
    });
